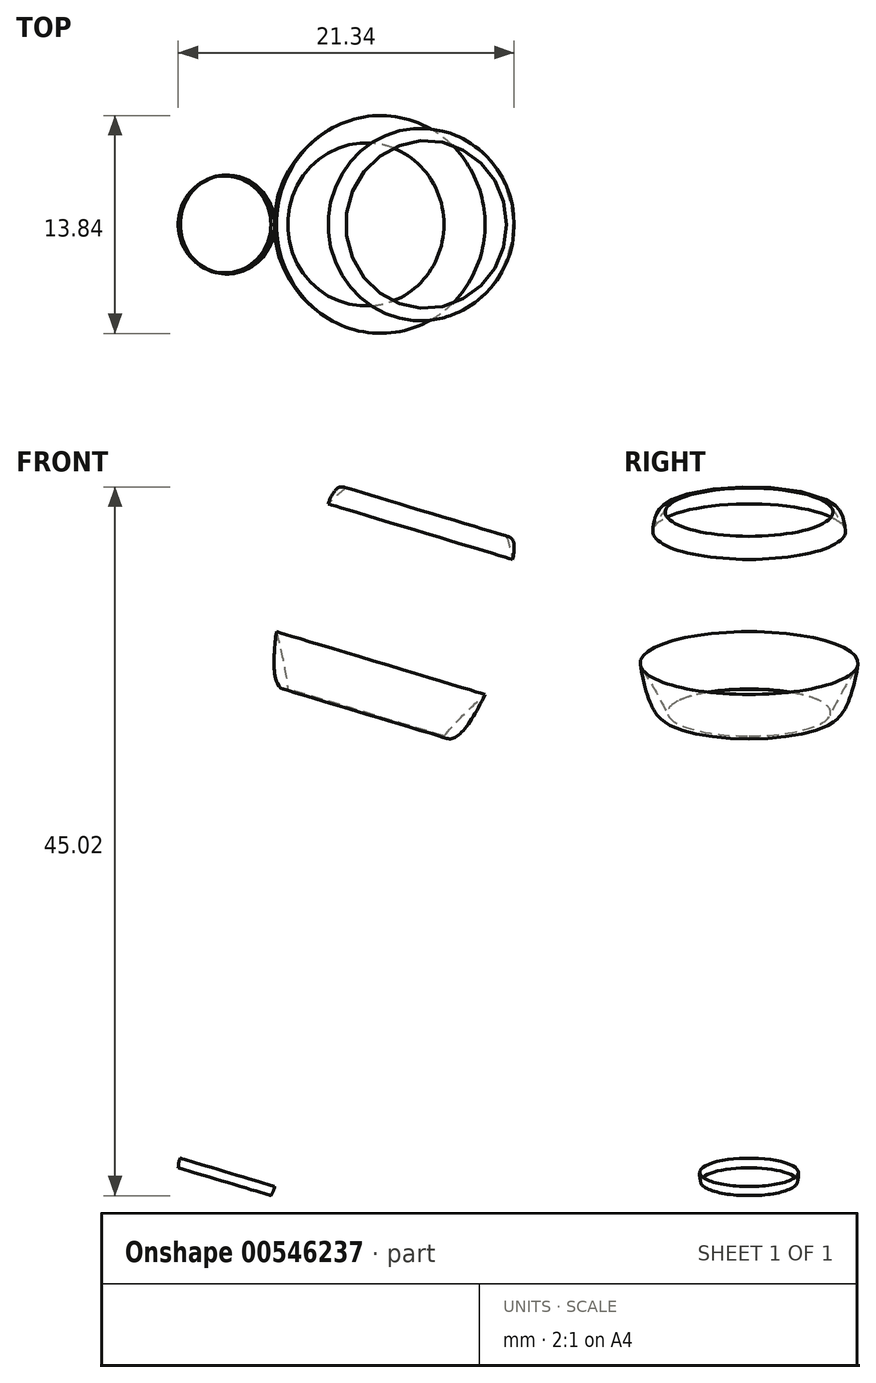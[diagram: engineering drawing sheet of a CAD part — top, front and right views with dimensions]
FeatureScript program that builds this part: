
annotation { "Feature Type Name" : "Feature", "Feature Type Description" : "" }
export const myFeature = defineFeature(function(context is Context, id is Id, definition is map)
    precondition{}
    {
        {
            var Q0;
            Q0=qCreatedBy(makeId("Front.planeOp"),FACE);
            var sketch = newSketch(context, id + "F0", { "sketchPlane" : qUnion([Q0])});
            skFitSpline(sketch, "E0", {"points": [v(-1.33, -3.07) * mm, v(-0.91, 0.51) * mm, v(0.15, 3.87) * mm, v(1.74, 8.17) * mm, v(4.12, 14.34) * mm, v(5.79, 20.45) * mm, v(5.32, 31.19) * mm, v(5.39, 37.22) * mm, v(12.42, 42.49) * mm, v(-1.33, -3.07) * mm]});
            skFitSpline(sketch, "E1", {"points": [v(-0.63, -2.97) * mm, v(-2.81, -2.24) * mm, v(11.65, 34.75) * mm, v(5.32, 29.18) * mm, v(6.25, 37.07) * mm, v(6.82, 36.92) * mm, v(8.6, 41.71) * mm, v(10.42, 40.5) * mm, v(13.75, 2.87) * mm, v(-0.63, -2.97) * mm]});
            skLineSegment(sketch, "E2", {"start": v(10.6, 22.2) * mm, "end": v(10.74, 22.03) * mm});
            skFitSpline(sketch, "E3", {"points": [v(-1.3, -1.23) * mm, v(-1.33, -3.07) * mm, v(0.15, -7.68) * mm, v(0.95, -8.33) * mm, v(3.11, -3.07) * mm, v(2.46, 0.81) * mm, v(-0.2, 1.14) * mm, v(-0.91, -0.35) * mm, v(-1.18, -0.62) * mm, v(-1.3, -1.23) * mm]});
            skLineSegment(sketch, "E4", {"start": v(11.65, 31.15) * mm, "end": v(1.17, -3.68) * mm, "construction": true});
            skLineSegment(sketch, "E5", {"start": v(-2.81, -2.24) * mm, "end": v(-1.33, -3.07) * mm});
            skSolve(sketch);
        }
        {
            var Q0;
            Q0=makeQuery(id+"F0.imprint","IMPRINT",FACE,{"disambiguationData":[TD([[makeQuery(id+"F0.imprint","IMPRINT",EDGE,{"derivedFrom":sQuery(id+"F0.wireOp",EDGE,"E0")}),1.0]])]});
            var Q1;
            Q1=sQuery(id+"F0.wireOp",EDGE,"E4");
            revolve(context, id + "F1", {"entities" : qUnion([Q0]), "axis" : qUnion([Q1]), "revolveType" : RevolveType.FULL});
        }
    });
